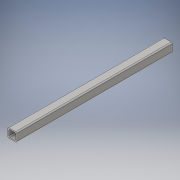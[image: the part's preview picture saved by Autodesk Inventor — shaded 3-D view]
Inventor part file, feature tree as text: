
AUTODESK INVENTOR PART (.ipt)
format: ipt  version: 2016 (Build 200138000, 138)  size: 113,152 bytes
history: native  units: in
note: dims shown in document units (in); Inventor stores cm internally (conversion verified against a paired STEP export)
features: extrude x1, sketch x1
ambient origin geometry x8: Origin, YZ Plane, XZ Plane, XY Plane, X Axis, Y Axis, Z Axis, Center Point
bodies: Solid1 (feature_tree)
feature tree (2):
  extrude  "Extrusion1"  Depth=1.0in
  sketch  "Sketch1"  dims[d0=1.0in d1=1.0in d2=0.125in d3=0.125in d4=17.25in d5=0.0in]
